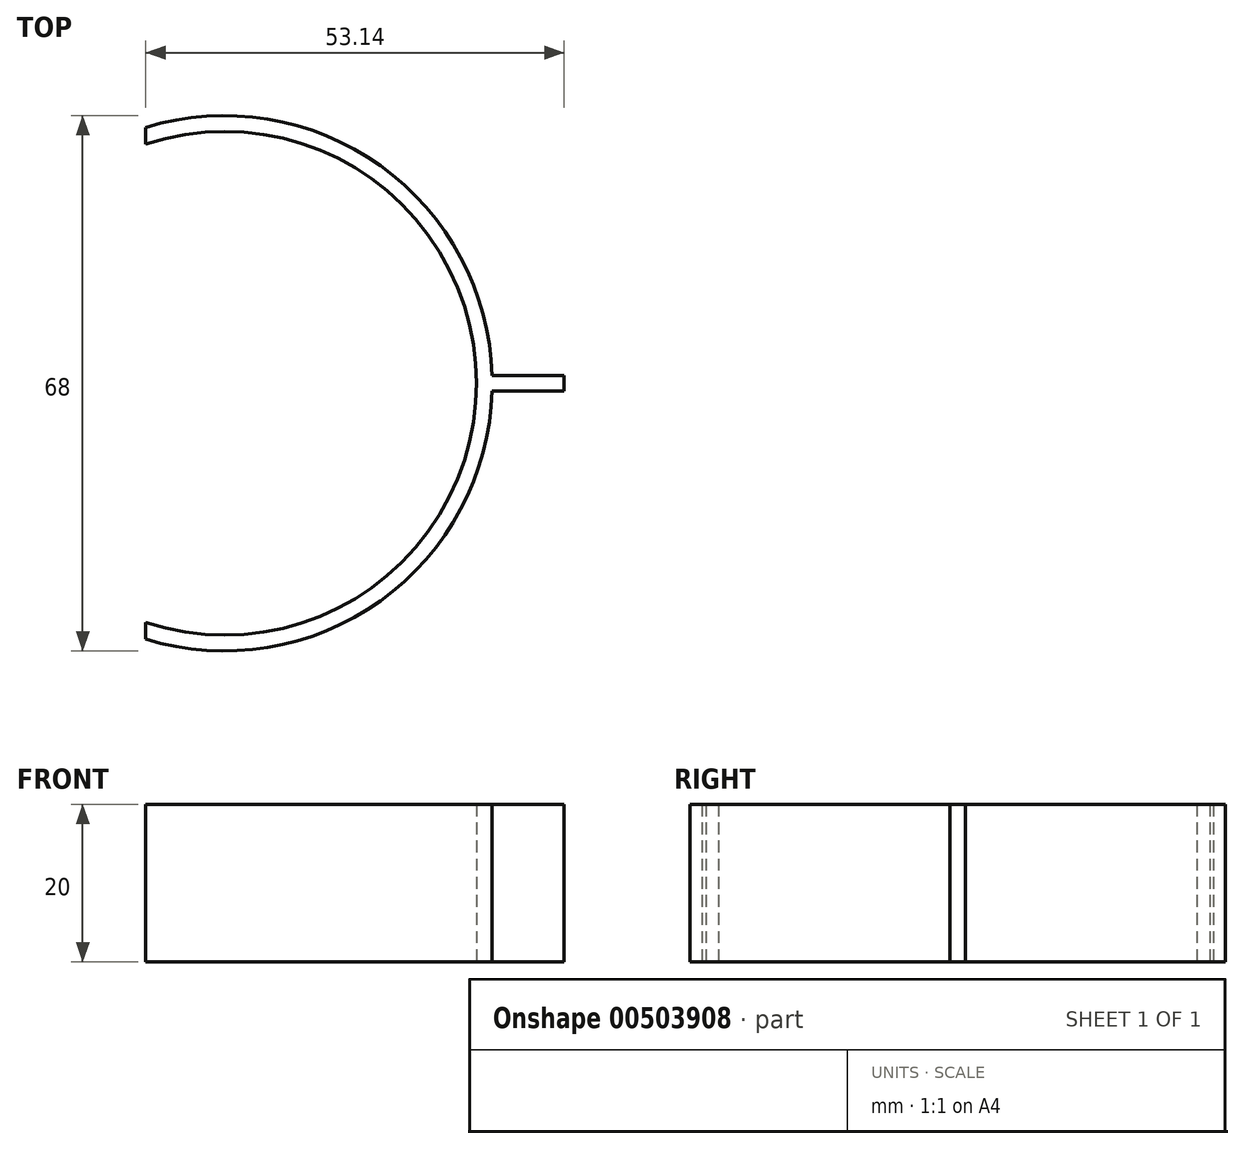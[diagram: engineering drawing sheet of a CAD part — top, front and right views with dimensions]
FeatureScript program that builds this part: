
annotation { "Feature Type Name" : "Feature", "Feature Type Description" : "" }
export const myFeature = defineFeature(function(context is Context, id is Id, definition is map)
    precondition{}
    {
        {
            var Q0;
            Q0=qCreatedBy(makeId("Top.planeOp"),FACE);
            var sketch = newSketch(context, id + "F0", { "sketchPlane" : qUnion([Q0])});
            skArc(sketch, "E0", {"start": v(-10, -30.4) * mm, "mid": v(32, 0) * mm, "end": v(-10, 30.4) * mm});
            skLineSegment(sketch, "E1", {"start": v(43.14, 1) * mm, "end": v(43.14, -1) * mm});
            skLineSegment(sketch, "E2", {"start": v(43.14, -1) * mm, "end": v(33.99, -1) * mm});
            skArc(sketch, "E3", {"start": v(33.99, 1) * mm, "mid": v(19.8, 27.64) * mm, "end": v(-10, 32.5) * mm});
            skLineSegment(sketch, "E4.trimOffspring", {"start": v(33.99, 1) * mm, "end": v(43.14, 1) * mm});
            skLineSegment(sketch, "E5", {"start": v(-10, 32.5) * mm, "end": v(-10, 30.4) * mm});
            skArc(sketch, "E6.trimOffspring", {"start": v(-10, -32.5) * mm, "mid": v(19.8, -27.64) * mm, "end": v(33.99, -1) * mm});
            skPoint(sketch, "E7.orphan", {"position": v(-10, -57.17) * mm});
            skLineSegment(sketch, "E8.trimOffspring", {"start": v(-10, -30.4) * mm, "end": v(-10, -32.5) * mm});
            skSolve(sketch);
        }
        {
            var Q0;
            Q0=makeQuery(id+"F0.imprint","IMPRINT",FACE,{"disambiguationData":[TD([[makeQuery(id+"F0.imprint","IMPRINT",EDGE,{"derivedFrom":sQuery(id+"F0.wireOp",EDGE,"E0")}),-1.0]])]});
            extrude(context, id + "F1", {"entities" : qUnion([Q0]), "depth" : 20 * mm});
        }
    });
